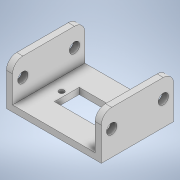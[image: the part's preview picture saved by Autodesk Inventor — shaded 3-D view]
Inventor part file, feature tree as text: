
AUTODESK INVENTOR PART (.ipt)
format: ipt  version: 2021 (Build 250183000, 183)  size: 139,776 bytes
history: native  units: mm
features: extrude x5, sketch x3, other x1, fillet x1
ambient origin geometry x8: Origin, YZ Plane, XZ Plane, XY Plane, X Axis, Y Axis, Z Axis, Center Point
bodies: Body1 (feature_tree)
feature tree (10):
  other  "Sólido1"
  extrude  "Extrusión1"  Depth=35.0mm TaperAngle=0.0deg
  sketch  "Boceto2"  dims[d15=60.0mm d16=0.0mm d17=5.0mm]
  extrude  "Extrusión2"  Depth=5.0mm
  extrude  "Extrusión3"  Depth=60.0mm TaperAngle=0.0deg
  fillet  "Empalme1"  [1 undecoded]
  sketch  "Boceto3"  dims[d29=60.0mm d30=0.0mm d31=60.0mm d32=0.0mm]
  extrude  "Extrusión4"  [1 undecoded]
  extrude  "Extrusión5"  [1 undecoded]
  sketch  "Boceto1"  dims[d6=35.0mm d7=0.0mm d13=60.0mm d14=0.0mm]
note: 3 required parameter values undecoded (feature->parameter linkage not recoverable at this tier; creation-order binding heuristic only, values carry confidence <= 0.55)
